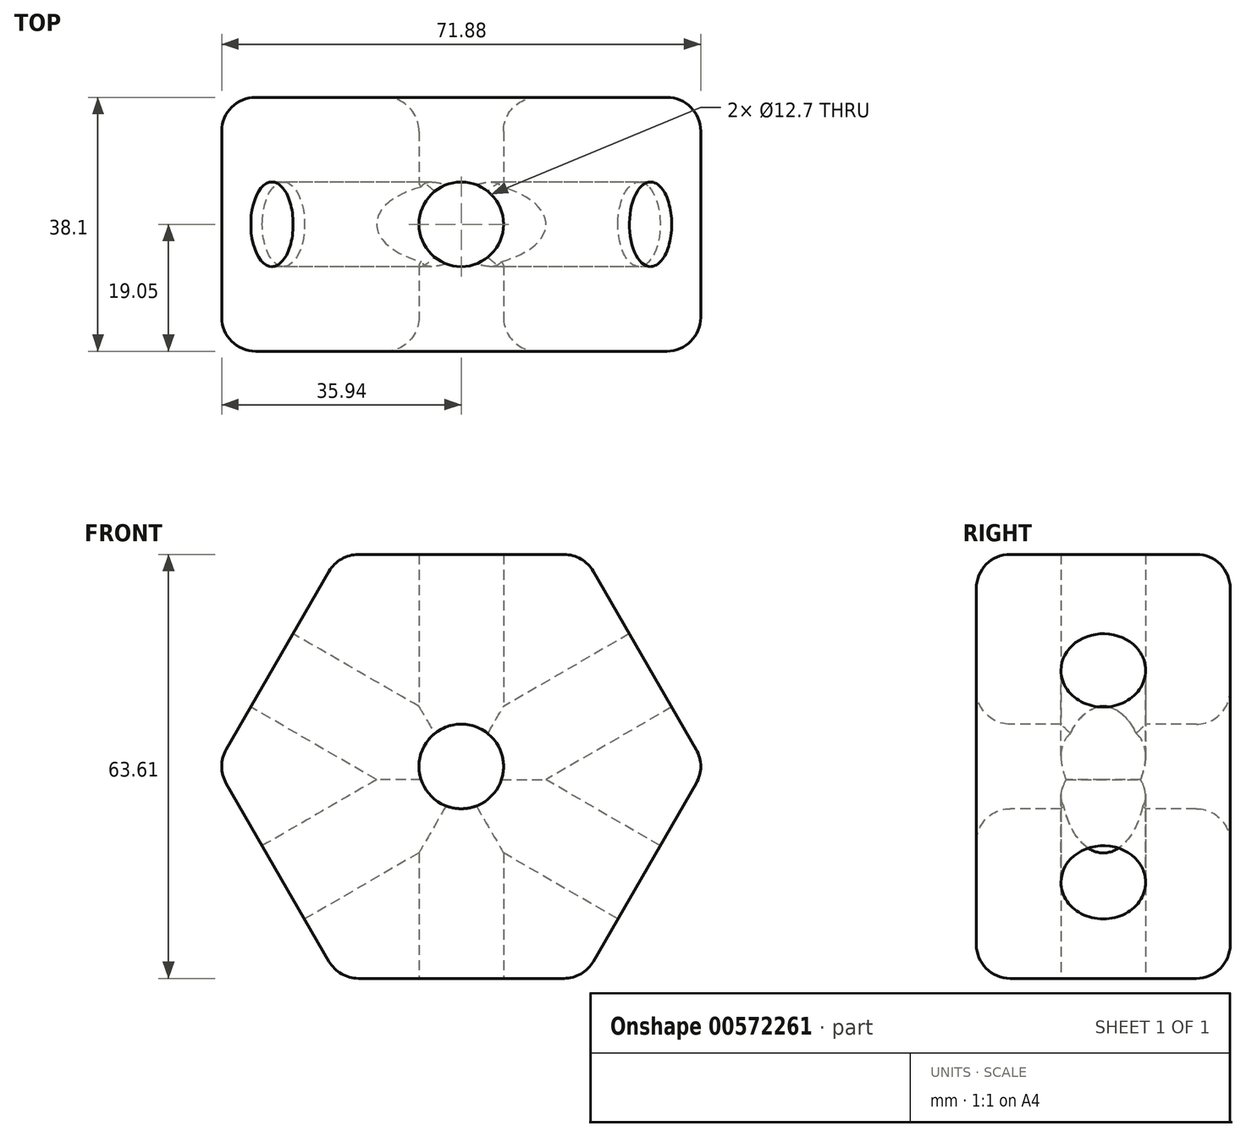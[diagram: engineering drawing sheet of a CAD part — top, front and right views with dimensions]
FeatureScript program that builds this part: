
annotation { "Feature Type Name" : "Feature", "Feature Type Description" : "" }
export const myFeature = defineFeature(function(context is Context, id is Id, definition is map)
    precondition{}
    {
        {
            var Q0;
            Q0=qCreatedBy(makeId("Front.planeOp"),FACE);
            var sketch = newSketch(context, id + "F0", { "sketchPlane" : qUnion([Q0])});
            skCircle(sketch, "E0.cCircle", {"center": v(0, 1.99) * mm, "radius": 31.8 * mm, "construction": true});
            skLineSegment(sketch, "E0.0", {"start": v(-18.36, 33.8) * mm, "end": v(18.36, 33.8) * mm});
            skLineSegment(sketch, "E0.1", {"start": v(18.36, 33.8) * mm, "end": v(36.73, 1.99) * mm});
            skLineSegment(sketch, "E0.2", {"start": v(36.73, 1.99) * mm, "end": v(18.36, -29.82) * mm});
            skLineSegment(sketch, "E0.3", {"start": v(18.36, -29.82) * mm, "end": v(-18.36, -29.82) * mm});
            skLineSegment(sketch, "E0.4", {"start": v(-18.36, -29.82) * mm, "end": v(-36.73, 1.99) * mm});
            skLineSegment(sketch, "E0.5", {"start": v(-36.73, 1.99) * mm, "end": v(-18.36, 33.8) * mm});
            skPoint(sketch, "E0.0.midPoint", {"position": v(0, 33.8) * mm});
            skSolve(sketch);
        }
        {
            var Q0;
            Q0 = qSketchRegion(id + "F0", true);
            extrude(context, id + "F1", {"entities" : qUnion([Q0]), "depth" : 38.1 * mm, "offsetDistance" : 25.4 * mm});
        }
        {
            var Q0;
            Q0=makeQuery(id+"F1.opExtrude","CAP_FACE",FACE,{"disambiguationData":[OSD([sQuery(id+"F0.wireOp",EDGE,"E0.0"),sQuery(id+"F0.wireOp",EDGE,"E0.1"),sQuery(id+"F0.wireOp",EDGE,"E0.2"),sQuery(id+"F0.wireOp",EDGE,"E0.3"),sQuery(id+"F0.wireOp",EDGE,"E0.4"),sQuery(id+"F0.wireOp",EDGE,"E0.5")])],"isStart":false});
            var sketch = newSketch(context, id + "F2", { "sketchPlane" : qUnion([Q0])});
            skPoint(sketch, "E1", {"position": v(0, 1.99) * mm});
            skSolve(sketch);
        }
        {
            var Q0;
            Q0=sQuery(id+"F2.wireOp",VERTEX,"E1");
            var Q1;
            Q1=makeQuery(id+"F1.opExtrude","SWEPT_BODY",BODY,{"disambiguationData":[OSD([sQuery(id+"F0.wireOp",EDGE,"E0.0"),sQuery(id+"F0.wireOp",EDGE,"E0.1"),sQuery(id+"F0.wireOp",EDGE,"E0.2"),sQuery(id+"F0.wireOp",EDGE,"E0.3"),sQuery(id+"F0.wireOp",EDGE,"E0.4"),sQuery(id+"F0.wireOp",EDGE,"E0.5")])]});
            hole(context, id + "F3", {"style" : HoleStyle.SIMPLE, "endStyle" : HoleEndStyle.THROUGH, "holeDiameter" : 12.7 * mm, "isTappedThrough" : true, "tappedDepth" : 12.7 * mm, "tapClearance" : 3, "locations" : qUnion([Q0]), "scope" : qUnion([Q1])});
        }
        {
            var Q0;
            Q0=makeQuery(id+"F1.opExtrude","CAP_EDGE",EDGE,{"disambiguationData":[OSD([sQuery(id+"F0.wireOp",EDGE,"E0.5")])],"isStart":false});
            var Q1;
            Q1=makeQuery(id+"F1.opExtrude","CAP_EDGE",EDGE,{"disambiguationData":[OSD([sQuery(id+"F0.wireOp",EDGE,"E0.0")])],"isStart":false});
            var Q2;
            Q2=makeQuery(id+"F1.opExtrude","CAP_FACE",FACE,{"disambiguationData":[OSD([sQuery(id+"F0.wireOp",EDGE,"E0.0"),sQuery(id+"F0.wireOp",EDGE,"E0.1"),sQuery(id+"F0.wireOp",EDGE,"E0.2"),sQuery(id+"F0.wireOp",EDGE,"E0.3"),sQuery(id+"F0.wireOp",EDGE,"E0.4"),sQuery(id+"F0.wireOp",EDGE,"E0.5")])],"isStart":false});
            var Q3;
            Q3=makeQuery(id+"F1.opExtrude","CAP_EDGE",EDGE,{"disambiguationData":[OSD([sQuery(id+"F0.wireOp",EDGE,"E0.3")])],"isStart":true});
            var Q4;
            Q4=makeQuery(id+"F1.opExtrude","CAP_EDGE",EDGE,{"disambiguationData":[OSD([sQuery(id+"F0.wireOp",EDGE,"E0.2")])],"isStart":true});
            var Q5;
            Q5=makeQuery(id+"F1.opExtrude","CAP_FACE",FACE,{"disambiguationData":[OSD([sQuery(id+"F0.wireOp",EDGE,"E0.0"),sQuery(id+"F0.wireOp",EDGE,"E0.1"),sQuery(id+"F0.wireOp",EDGE,"E0.2"),sQuery(id+"F0.wireOp",EDGE,"E0.3"),sQuery(id+"F0.wireOp",EDGE,"E0.4"),sQuery(id+"F0.wireOp",EDGE,"E0.5")])],"isStart":true});
            var Q6;
            Q6=makeQuery(id+"F1.opExtrude","SWEPT_EDGE",EDGE,{"disambiguationData":[OSD([sQuery(id+"F0.wireOp",EDGE,"E0.3"),sQuery(id+"F0.wireOp",EDGE,"E0.4")])]});
            var Q7;
            Q7=makeQuery(id+"F1.opExtrude","SWEPT_EDGE",EDGE,{"disambiguationData":[OSD([sQuery(id+"F0.wireOp",EDGE,"E0.0"),sQuery(id+"F0.wireOp",EDGE,"E0.5")])]});
            var Q8;
            Q8=makeQuery(id+"F1.opExtrude","SWEPT_EDGE",EDGE,{"disambiguationData":[OSD([sQuery(id+"F0.wireOp",EDGE,"E0.4"),sQuery(id+"F0.wireOp",EDGE,"E0.5")])]});
            var Q9;
            Q9=makeQuery(id+"F1.opExtrude","SWEPT_EDGE",EDGE,{"disambiguationData":[OSD([sQuery(id+"F0.wireOp",EDGE,"E0.0"),sQuery(id+"F0.wireOp",EDGE,"E0.1")])]});
            var Q10;
            Q10=makeQuery(id+"F1.opExtrude","SWEPT_EDGE",EDGE,{"disambiguationData":[OSD([sQuery(id+"F0.wireOp",EDGE,"E0.2"),sQuery(id+"F0.wireOp",EDGE,"E0.3")])]});
            var Q11;
            Q11=makeQuery(id+"F1.opExtrude","SWEPT_EDGE",EDGE,{"disambiguationData":[OSD([sQuery(id+"F0.wireOp",EDGE,"E0.1"),sQuery(id+"F0.wireOp",EDGE,"E0.2")])]});
            fillet(context, id + "F4", {"entities" : qUnion([Q0, Q1, Q2, Q3, Q4, Q5, Q6, Q7, Q8, Q9, Q10, Q11]), "radius" : 5.08 * mm, "tangentPropagation" : true, "allowEdgeOverflow" : false});
        }
        {
            var Q0;
            Q0=makeQuery(id+"F1.opExtrude","SWEPT_FACE",FACE,{"disambiguationData":[OSD([sQuery(id+"F0.wireOp",EDGE,"E0.5")])]});
            var sketch = newSketch(context, id + "F5", { "sketchPlane" : qUnion([Q0])});
            skPoint(sketch, "E2", {"position": v(19.05, 0) * mm});
            skPoint(sketch, "E2.positionSnap0", {"position": v(19.05, 17.15) * mm});
            skSolve(sketch);
        }
        {
            var Q0;
            Q0=sQuery(id+"F5.wireOp",VERTEX,"E2");
            var Q1;
            Q1=makeQuery(id+"F1.opExtrude","SWEPT_BODY",BODY,{"disambiguationData":[OSD([sQuery(id+"F0.wireOp",EDGE,"E0.0"),sQuery(id+"F0.wireOp",EDGE,"E0.1"),sQuery(id+"F0.wireOp",EDGE,"E0.2"),sQuery(id+"F0.wireOp",EDGE,"E0.3"),sQuery(id+"F0.wireOp",EDGE,"E0.4"),sQuery(id+"F0.wireOp",EDGE,"E0.5")])]});
            hole(context, id + "F6", {"style" : HoleStyle.SIMPLE, "endStyle" : HoleEndStyle.THROUGH, "holeDiameter" : 12.7 * mm, "isTappedThrough" : true, "tappedDepth" : 12.7 * mm, "tapClearance" : 3, "locations" : qUnion([Q0]), "scope" : qUnion([Q1])});
        }
        {
            var Q0;
            Q0=makeQuery(id+"F1.opExtrude","SWEPT_FACE",FACE,{"disambiguationData":[OSD([sQuery(id+"F0.wireOp",EDGE,"E0.4")])]});
            var sketch = newSketch(context, id + "F7", { "sketchPlane" : qUnion([Q0])});
            skPoint(sketch, "E3", {"position": v(19.05, 0) * mm});
            skPoint(sketch, "E3.positionSnap0", {"position": v(19.05, 17.15) * mm});
            skSolve(sketch);
        }
        {
            var Q0;
            Q0=sQuery(id+"F7.wireOp",VERTEX,"E3");
            var Q1;
            Q1=makeQuery(id+"F1.opExtrude","SWEPT_BODY",BODY,{"disambiguationData":[OSD([sQuery(id+"F0.wireOp",EDGE,"E0.0"),sQuery(id+"F0.wireOp",EDGE,"E0.1"),sQuery(id+"F0.wireOp",EDGE,"E0.2"),sQuery(id+"F0.wireOp",EDGE,"E0.3"),sQuery(id+"F0.wireOp",EDGE,"E0.4"),sQuery(id+"F0.wireOp",EDGE,"E0.5")])]});
            hole(context, id + "F8", {"style" : HoleStyle.SIMPLE, "endStyle" : HoleEndStyle.THROUGH, "holeDiameter" : 12.7 * mm, "isTappedThrough" : true, "tappedDepth" : 12.7 * mm, "tapClearance" : 3, "locations" : qUnion([Q0]), "scope" : qUnion([Q1])});
        }
        {
            var Q0;
            Q0=makeQuery(id+"F1.opExtrude","SWEPT_FACE",FACE,{"disambiguationData":[OSD([sQuery(id+"F0.wireOp",EDGE,"E0.3")])]});
            var sketch = newSketch(context, id + "F9", { "sketchPlane" : qUnion([Q0])});
            skPoint(sketch, "E4", {"position": v(0, 19.05) * mm});
            skPoint(sketch, "E4.positionSnap0", {"position": v(15.43, 19.05) * mm});
            skSolve(sketch);
        }
        {
            var Q0;
            Q0=sQuery(id+"F9.wireOp",VERTEX,"E4");
            var Q1;
            Q1=makeQuery(id+"F1.opExtrude","SWEPT_BODY",BODY,{"disambiguationData":[OSD([sQuery(id+"F0.wireOp",EDGE,"E0.0"),sQuery(id+"F0.wireOp",EDGE,"E0.1"),sQuery(id+"F0.wireOp",EDGE,"E0.2"),sQuery(id+"F0.wireOp",EDGE,"E0.3"),sQuery(id+"F0.wireOp",EDGE,"E0.4"),sQuery(id+"F0.wireOp",EDGE,"E0.5")])]});
            hole(context, id + "F10", {"style" : HoleStyle.SIMPLE, "endStyle" : HoleEndStyle.THROUGH, "holeDiameter" : 12.7 * mm, "isTappedThrough" : true, "tappedDepth" : 12.7 * mm, "tapClearance" : 3, "locations" : qUnion([Q0]), "scope" : qUnion([Q1])});
        }
    });
